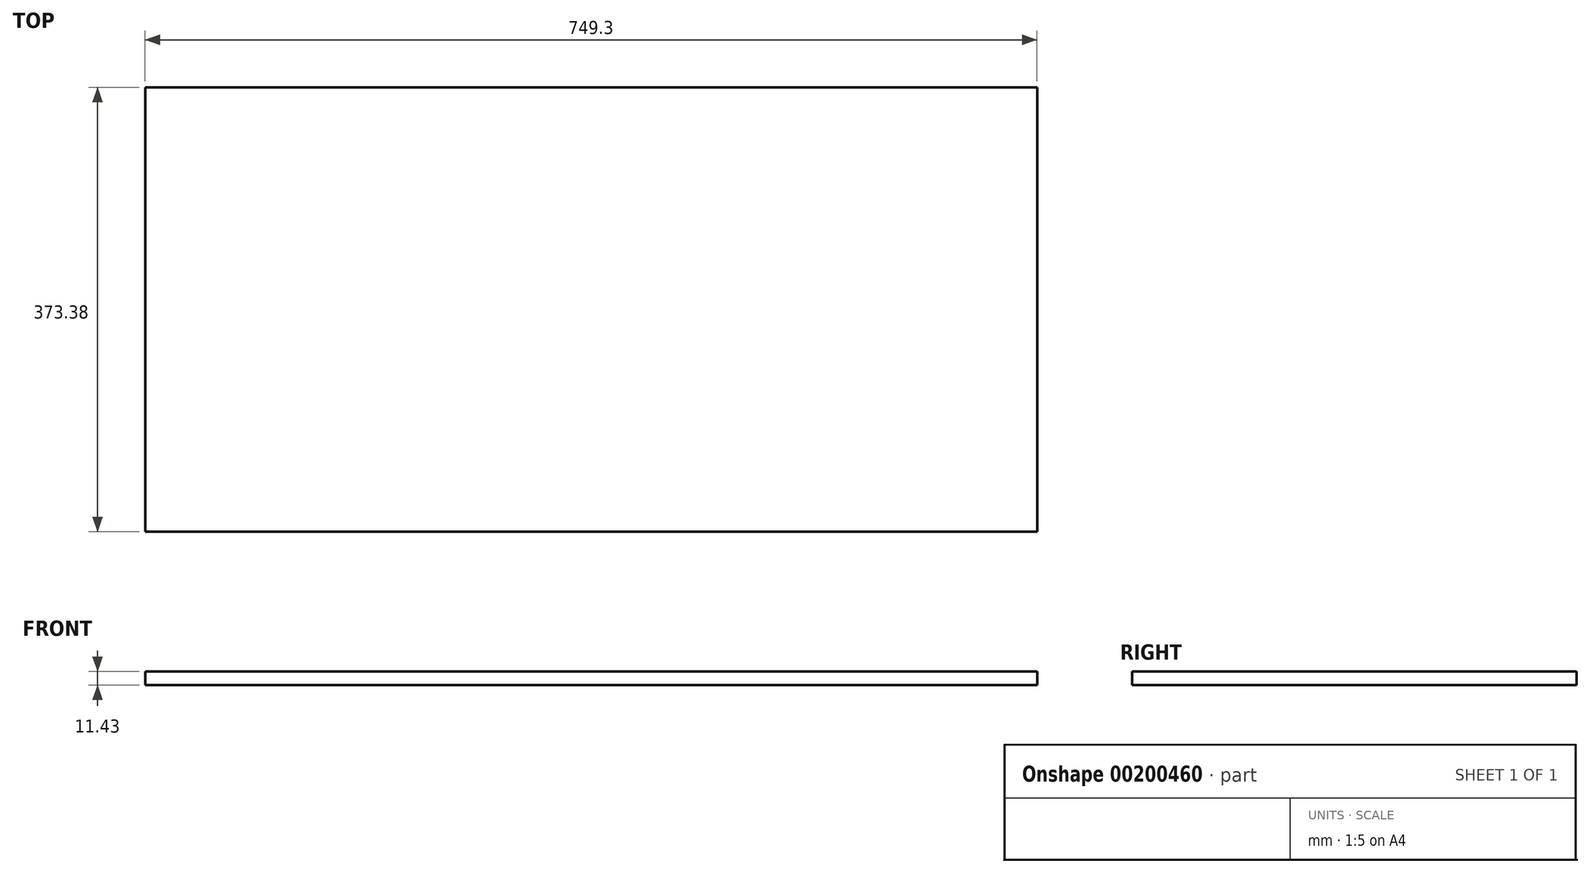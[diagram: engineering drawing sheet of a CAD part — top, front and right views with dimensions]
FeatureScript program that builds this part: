
annotation { "Feature Type Name" : "Feature", "Feature Type Description" : "" }
export const myFeature = defineFeature(function(context is Context, id is Id, definition is map)
    precondition{}
    {
        {
            var Q0;
            Q0=qCreatedBy(makeId("Top.planeOp"),FACE);
            var sketch = newSketch(context, id + "F0", { "sketchPlane" : qUnion([Q0])});
            skLineSegment(sketch, "E0.bottom", {"start": v(-1014.48, 138.63) * mm, "end": v(-265.18, 138.63) * mm});
            skLineSegment(sketch, "E0.top", {"start": v(-1014.48, -234.75) * mm, "end": v(-265.18, -234.75) * mm});
            skLineSegment(sketch, "E0.left", {"start": v(-1014.48, 138.63) * mm, "end": v(-1014.48, -234.75) * mm});
            skLineSegment(sketch, "E0.right", {"start": v(-265.18, 138.63) * mm, "end": v(-265.18, -234.75) * mm});
            skSolve(sketch);
        }
        {
            var Q0;
            Q0 = qSketchRegion(id + "F0", true);
            extrude(context, id + "F1", {"entities" : qUnion([Q0]), "depth" : 11.43 * mm});
        }
    });
